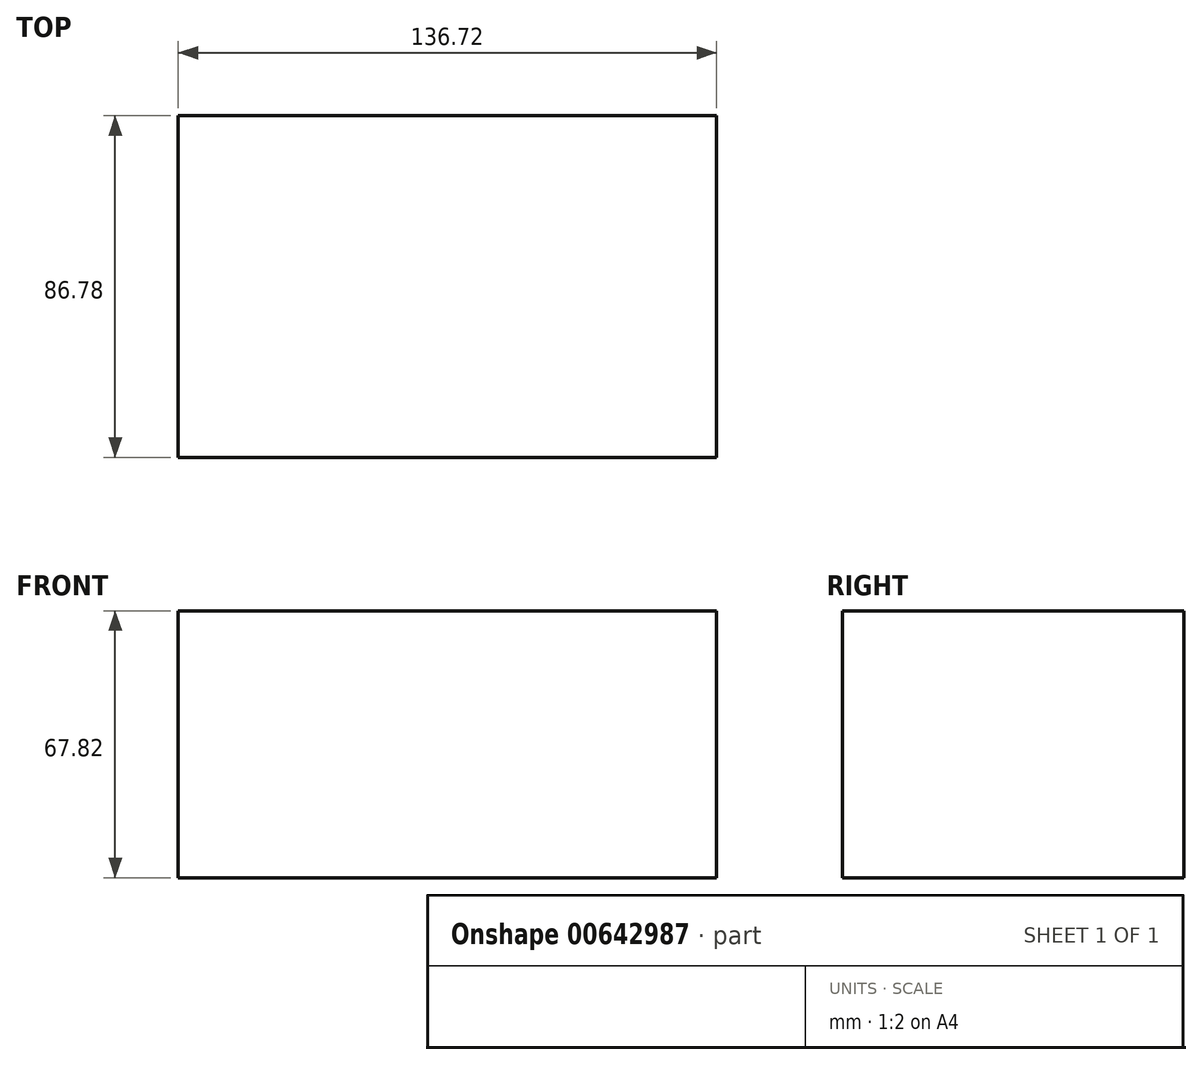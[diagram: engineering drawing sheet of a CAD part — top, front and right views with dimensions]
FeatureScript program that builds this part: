
annotation { "Feature Type Name" : "Feature", "Feature Type Description" : "" }
export const myFeature = defineFeature(function(context is Context, id is Id, definition is map)
    precondition{}
    {
        {
            var Q0;
            Q0=qCreatedBy(makeId("Top.planeOp"),FACE);
            var sketch = newSketch(context, id + "F0", { "sketchPlane" : qUnion([Q0])});
            skLineSegment(sketch, "E0.bottom", {"start": v(-69.77, 35.58) * mm, "end": v(66.95, 35.58) * mm});
            skLineSegment(sketch, "E0.top", {"start": v(-69.77, -51.2) * mm, "end": v(66.95, -51.2) * mm});
            skLineSegment(sketch, "E0.left", {"start": v(-69.77, 35.58) * mm, "end": v(-69.77, -51.2) * mm});
            skLineSegment(sketch, "E0.right", {"start": v(66.95, 35.58) * mm, "end": v(66.95, -51.2) * mm});
            skSolve(sketch);
        }
        {
            var Q0;
            Q0 = qSketchRegion(id + "F0", true);
            extrude(context, id + "F1", {"entities" : qUnion([Q0]), "depth" : 67.82 * mm, "offsetDistance" : 25.4 * mm});
        }
    });
